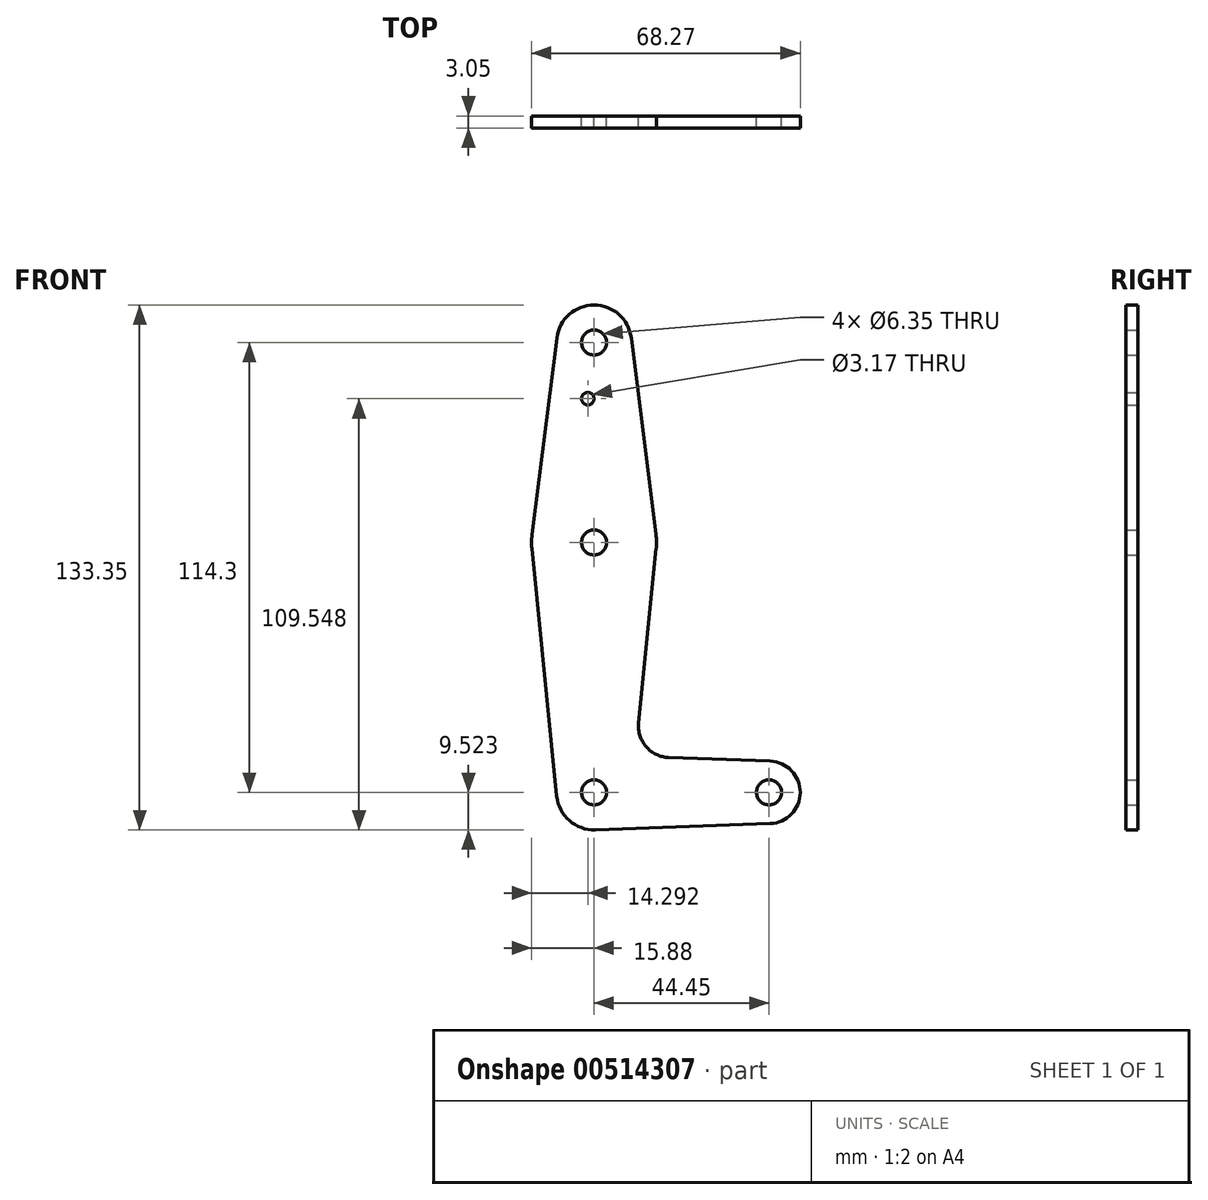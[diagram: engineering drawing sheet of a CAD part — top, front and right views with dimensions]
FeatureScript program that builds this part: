
annotation { "Feature Type Name" : "Feature", "Feature Type Description" : "" }
export const myFeature = defineFeature(function(context is Context, id is Id, definition is map)
    precondition{}
    {
        {
            var Q0;
            Q0=qCreatedBy(makeId("Front.planeOp"),FACE);
            var sketch = newSketch(context, id + "F0", { "sketchPlane" : qUnion([Q0])});
            skLineSegment(sketch, "E0", {"start": v(-54.68, 98.66) * mm, "end": v(-54.68, -15.64) * mm, "construction": true});
            skLineSegment(sketch, "E1", {"start": v(-54.68, -15.64) * mm, "end": v(-10.23, -15.64) * mm, "construction": true});
            skCircle(sketch, "E2", {"center": v(-54.68, 98.66) * mm, "radius": 9.53 * mm});
            skCircle(sketch, "E3", {"center": v(-54.68, -15.64) * mm, "radius": 9.53 * mm});
            skCircle(sketch, "E4", {"center": v(-10.23, -15.64) * mm, "radius": 7.94 * mm});
            skCircle(sketch, "E5", {"center": v(-54.68, 47.86) * mm, "radius": 15.88 * mm});
            skLineSegment(sketch, "E6", {"start": v(-45.23, 99.85) * mm, "end": v(-38.93, 49.85) * mm});
            skLineSegment(sketch, "E7", {"start": v(-64.13, 99.85) * mm, "end": v(-70.43, 49.85) * mm});
            skLineSegment(sketch, "E8", {"start": v(-38.89, 46.28) * mm, "end": v(-43.34, 1.96) * mm});
            skLineSegment(sketch, "E9", {"start": v(-70.48, 46.28) * mm, "end": v(-64.16, -16.59) * mm});
            skLineSegment(sketch, "E10", {"start": v(-35.71, -6.78) * mm, "end": v(-9.95, -7.7) * mm});
            skLineSegment(sketch, "E11", {"start": v(-54.34, -25.16) * mm, "end": v(-9.95, -23.57) * mm});
            skCircle(sketch, "E12", {"center": v(-56.27, 84.39) * mm, "radius": 1.59 * mm});
            skCircle(sketch, "E13", {"center": v(-54.68, 98.66) * mm, "radius": 3.18 * mm});
            skCircle(sketch, "E14", {"center": v(-54.68, 47.86) * mm, "radius": 3.18 * mm});
            skCircle(sketch, "E15", {"center": v(-54.68, -15.64) * mm, "radius": 3.18 * mm});
            skCircle(sketch, "E16", {"center": v(-10.23, -15.64) * mm, "radius": 3.18 * mm});
            skArc(sketch, "E17.filletArc", {"start": v(-43.34, 1.96) * mm, "mid": v(-41.42, -4.07) * mm, "end": v(-35.71, -6.78) * mm});
            skSolve(sketch);
        }
        {
            var Q0;
            {var subQ0=sQuery(id+"F0.wireOp",EDGE,"E6");Q0=makeQuery(id+"F0.imprint","IMPRINT",FACE,{"disambiguationData":[TD([[makeQuery(id+"F0.imprint","IMPRINT",EDGE,{"derivedFrom":subQ0}),-1.0]])]});}
            var Q1;
            {var subQ0=sQuery(id+"F0.wireOp",EDGE,"E8");Q1=makeQuery(id+"F0.imprint","IMPRINT",FACE,{"disambiguationData":[TD([[makeQuery(id+"F0.imprint","IMPRINT",EDGE,{"derivedFrom":subQ0}),-1.0]])]});}
            var Q2;
            Q2=makeQuery(id+"F0.imprint","IMPRINT",FACE,{"disambiguationData":[TD([[makeQuery(id+"F0.imprint","IMPRINT",EDGE,{"derivedFrom":sQuery(id+"F0.wireOp",EDGE,"E13")}),-1.0]])]});
            var Q3;
            Q3=makeQuery(id+"F0.imprint","IMPRINT",FACE,{"disambiguationData":[TD([[makeQuery(id+"F0.imprint","IMPRINT",EDGE,{"derivedFrom":sQuery(id+"F0.wireOp",EDGE,"E14")}),-1.0]])]});
            var Q4;
            Q4=makeQuery(id+"F0.imprint","IMPRINT",FACE,{"disambiguationData":[TD([[makeQuery(id+"F0.imprint","IMPRINT",EDGE,{"derivedFrom":sQuery(id+"F0.wireOp",EDGE,"E15")}),-1.0]])]});
            var Q5;
            Q5=makeQuery(id+"F0.imprint","IMPRINT",FACE,{"disambiguationData":[TD([[makeQuery(id+"F0.imprint","IMPRINT",EDGE,{"derivedFrom":sQuery(id+"F0.wireOp",EDGE,"E16")}),-1.0]])]});
            extrude(context, id + "F1", {"entities" : qUnion([Q0, Q1, Q2, Q3, Q4, Q5]), "depth" : 3.05 * mm, "offsetDistance" : 25.4 * mm});
        }
    });
